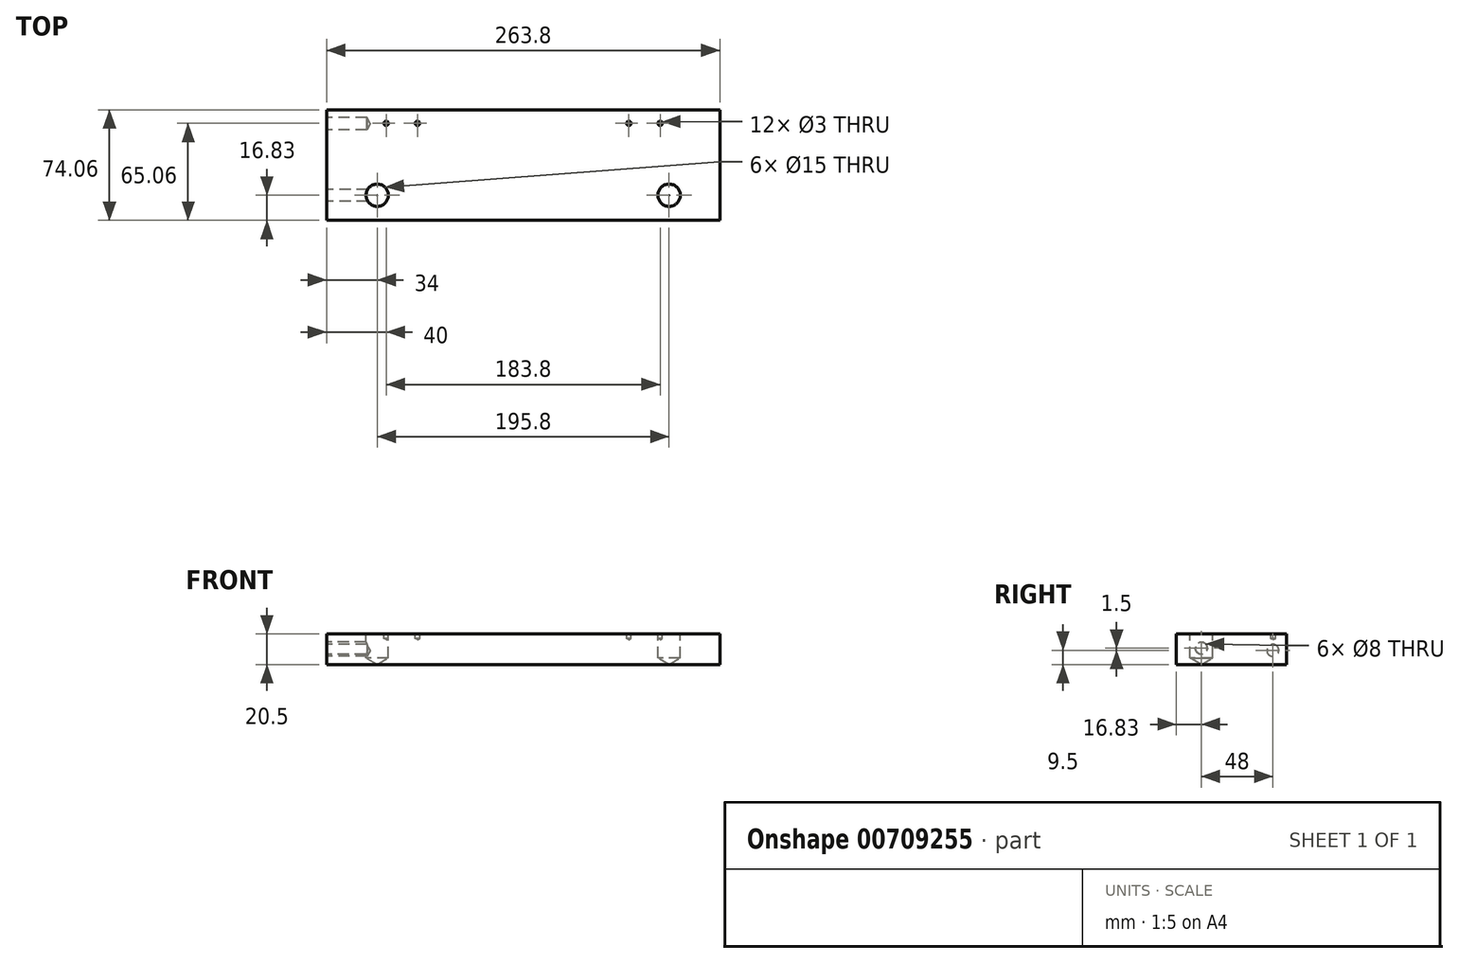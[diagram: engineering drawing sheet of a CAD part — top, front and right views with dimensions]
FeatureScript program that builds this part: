
annotation { "Feature Type Name" : "Feature", "Feature Type Description" : "" }
export const myFeature = defineFeature(function(context is Context, id is Id, definition is map)
    precondition{}
    {
        {
            var Q0;
            Q0=qCreatedBy(makeId("Top.planeOp"),FACE);
            var sketch = newSketch(context, id + "F0", { "sketchPlane" : qUnion([Q0])});
            skLineSegment(sketch, "E0.bottom", {"start": v(131.9, -37.03) * mm, "end": v(-131.9, -37.03) * mm});
            skLineSegment(sketch, "E0.top", {"start": v(131.9, 37.03) * mm, "end": v(-131.9, 37.03) * mm});
            skLineSegment(sketch, "E0.left", {"start": v(131.9, -37.03) * mm, "end": v(131.9, 37.03) * mm});
            skLineSegment(sketch, "E0.right", {"start": v(-131.9, -37.03) * mm, "end": v(-131.9, 37.03) * mm});
            skPoint(sketch, "E0.middle", {"position": v(0, 0) * mm});
            skSolve(sketch);
        }
        {
            var Q0;
            Q0=makeQuery(id+"F0.imprint","IMPRINT",FACE,{"disambiguationData":[TD([[makeQuery(id+"F0.imprint","IMPRINT",EDGE,{"derivedFrom":sQuery(id+"F0.wireOp",EDGE,"E0.bottom")}),-1.0]])]});
            extrude(context, id + "F1", {"entities" : qUnion([Q0]), "depth" : 20.5 * mm, "offsetDistance" : 25 * mm});
        }
        {
            var Q0;
            Q0=makeQuery(id+"F1.opExtrude","CAP_FACE",FACE,{"disambiguationData":[OSD([sQuery(id+"F0.wireOp",EDGE,"E0.bottom"),sQuery(id+"F0.wireOp",EDGE,"E0.top"),sQuery(id+"F0.wireOp",EDGE,"E0.left"),sQuery(id+"F0.wireOp",EDGE,"E0.right")])],"isStart":false});
            var sketch = newSketch(context, id + "F2", { "sketchPlane" : qUnion([Q0])});
            skPoint(sketch, "E1", {"position": v(-91.9, 28.03) * mm});
            skPoint(sketch, "E2", {"position": v(-70.9, 28.03) * mm});
            skPoint(sketch, "E3", {"position": v(70.9, 28.03) * mm});
            skPoint(sketch, "E4", {"position": v(91.9, 28.03) * mm});
            skSolve(sketch);
        }
        {
            var Q0;
            Q0=sQuery(id+"F2.wireOp",VERTEX,"E1");
            var Q1;
            Q1=sQuery(id+"F2.wireOp",VERTEX,"E2");
            var Q2;
            Q2=sQuery(id+"F2.wireOp",VERTEX,"E3");
            var Q3;
            Q3=sQuery(id+"F2.wireOp",VERTEX,"E4");
            var Q4;
            Q4=makeQuery(id+"F1.opExtrude","SWEPT_BODY",BODY,{"disambiguationData":[OSD([sQuery(id+"F0.wireOp",EDGE,"E0.bottom"),sQuery(id+"F0.wireOp",EDGE,"E0.top"),sQuery(id+"F0.wireOp",EDGE,"E0.left"),sQuery(id+"F0.wireOp",EDGE,"E0.right")])]});
            hole(context, id + "F3", {"style" : HoleStyle.SIMPLE, "endStyle" : HoleEndStyle.BLIND, "holeDiameter" : 3 * mm, "majorDiameter" : 5 * mm, "holeDepth" : 3 * mm, "isTappedThrough" : true, "tappedDepth" : 12 * mm, "tapClearance" : 3, "startFromSketch" : true, "locations" : qUnion([Q0, Q1, Q2, Q3]), "scope" : qUnion([Q4])});
        }
        {
            var Q0;
            Q0=makeQuery(id+"F1.opExtrude","CAP_FACE",FACE,{"disambiguationData":[OSD([sQuery(id+"F0.wireOp",EDGE,"E0.bottom"),sQuery(id+"F0.wireOp",EDGE,"E0.top"),sQuery(id+"F0.wireOp",EDGE,"E0.left"),sQuery(id+"F0.wireOp",EDGE,"E0.right")])],"isStart":false});
            var sketch = newSketch(context, id + "F4", { "sketchPlane" : qUnion([Q0])});
            skPoint(sketch, "E5", {"position": v(-97.9, -20.2) * mm});
            skPoint(sketch, "E6", {"position": v(97.9, -20.2) * mm});
            skSolve(sketch);
        }
        {
            var Q0;
            Q0=sQuery(id+"F4.wireOp",VERTEX,"E5");
            var Q1;
            Q1=sQuery(id+"F4.wireOp",VERTEX,"E6");
            var Q2;
            Q2=makeQuery(id+"F1.opExtrude","SWEPT_BODY",BODY,{"disambiguationData":[OSD([sQuery(id+"F0.wireOp",EDGE,"E0.bottom"),sQuery(id+"F0.wireOp",EDGE,"E0.top"),sQuery(id+"F0.wireOp",EDGE,"E0.left"),sQuery(id+"F0.wireOp",EDGE,"E0.right")])]});
            hole(context, id + "F5", {"style" : HoleStyle.SIMPLE, "endStyle" : HoleEndStyle.BLIND, "holeDiameter" : 15 * mm, "majorDiameter" : 5 * mm, "holeDepth" : 16 * mm, "isTappedThrough" : true, "tappedDepth" : 12 * mm, "tapClearance" : 3, "startFromSketch" : true, "locations" : qUnion([Q0, Q1]), "scope" : qUnion([Q2])});
        }
        {
            var Q0;
            Q0=makeQuery(id+"F1.opExtrude","SWEPT_FACE",FACE,{"disambiguationData":[OSD([sQuery(id+"F0.wireOp",EDGE,"E0.right")])]});
            var sketch = newSketch(context, id + "F6", { "sketchPlane" : qUnion([Q0])});
            skPoint(sketch, "E7", {"position": v(20.2, 11) * mm});
            skSolve(sketch);
        }
        {
            var Q0;
            Q0=sQuery(id+"F6.wireOp",VERTEX,"E7");
            var Q1;
            Q1=makeQuery(id+"F1.opExtrude","SWEPT_BODY",BODY,{"disambiguationData":[OSD([sQuery(id+"F0.wireOp",EDGE,"E0.bottom"),sQuery(id+"F0.wireOp",EDGE,"E0.top"),sQuery(id+"F0.wireOp",EDGE,"E0.left"),sQuery(id+"F0.wireOp",EDGE,"E0.right")])]});
            hole(context, id + "F7", {"style" : HoleStyle.SIMPLE, "endStyle" : HoleEndStyle.BLIND, "holeDiameter" : 8 * mm, "majorDiameter" : 5 * mm, "holeDepth" : 34 * mm, "isTappedThrough" : true, "tappedDepth" : 12 * mm, "tapClearance" : 3, "startFromSketch" : true, "locations" : qUnion([Q0]), "scope" : qUnion([Q1])});
        }
        {
            var Q0;
            Q0=makeQuery(id+"F1.opExtrude","SWEPT_FACE",FACE,{"disambiguationData":[OSD([sQuery(id+"F0.wireOp",EDGE,"E0.right")])]});
            var sketch = newSketch(context, id + "F8", { "sketchPlane" : qUnion([Q0])});
            skPoint(sketch, "E8", {"position": v(-27.8, 9.5) * mm});
            skSolve(sketch);
        }
        {
            var Q0;
            Q0=sQuery(id+"F8.wireOp",VERTEX,"E8");
            var Q1;
            Q1=makeQuery(id+"F1.opExtrude","SWEPT_BODY",BODY,{"disambiguationData":[OSD([sQuery(id+"F0.wireOp",EDGE,"E0.bottom"),sQuery(id+"F0.wireOp",EDGE,"E0.top"),sQuery(id+"F0.wireOp",EDGE,"E0.left"),sQuery(id+"F0.wireOp",EDGE,"E0.right")])]});
            hole(context, id + "F9", {"style" : HoleStyle.SIMPLE, "endStyle" : HoleEndStyle.BLIND, "holeDiameter" : 8 * mm, "majorDiameter" : 5 * mm, "holeDepth" : 27 * mm, "isTappedThrough" : true, "tappedDepth" : 12 * mm, "tapClearance" : 3, "startFromSketch" : true, "locations" : qUnion([Q0]), "scope" : qUnion([Q1])});
        }
    });
